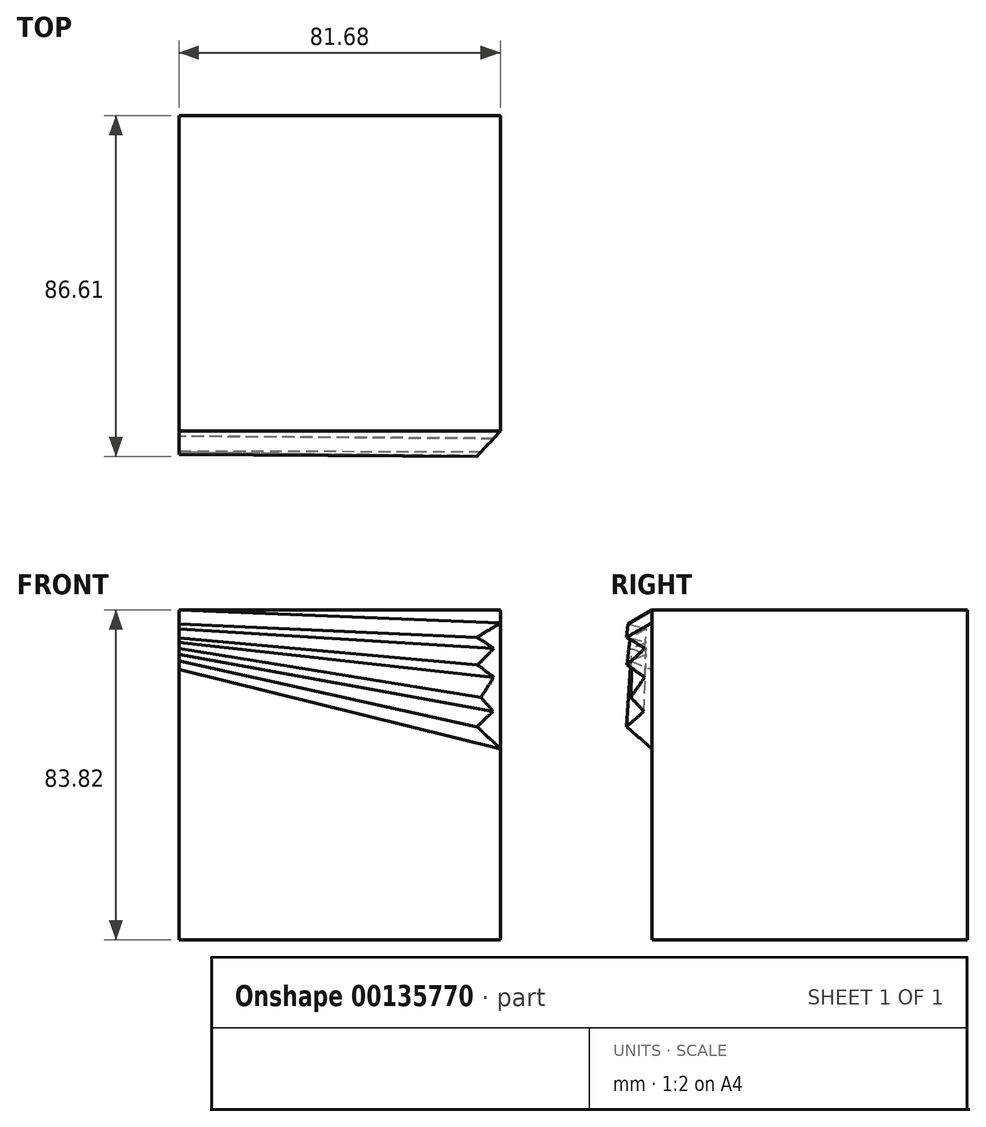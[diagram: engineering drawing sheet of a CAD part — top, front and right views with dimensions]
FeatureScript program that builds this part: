
annotation { "Feature Type Name" : "Feature", "Feature Type Description" : "" }
export const myFeature = defineFeature(function(context is Context, id is Id, definition is map)
    precondition{}
    {
        {
            var Q0;
            Q0=qCreatedBy(makeId("Top.planeOp"),FACE);
            var sketch = newSketch(context, id + "F0", { "sketchPlane" : qUnion([Q0])});
            skLineSegment(sketch, "E0.bottom", {"start": v(0, 0) * mm, "end": v(81.68, 0) * mm});
            skLineSegment(sketch, "E0.top", {"start": v(0, 80.12) * mm, "end": v(81.68, 80.12) * mm});
            skLineSegment(sketch, "E0.left", {"start": v(0, 0) * mm, "end": v(0, 80.12) * mm});
            skLineSegment(sketch, "E0.right", {"start": v(81.68, 0) * mm, "end": v(81.68, 80.12) * mm});
            skSolve(sketch);
        }
        {
            var Q0;
            Q0 = qSketchRegion(id + "F0", true);
            extrude(context, id + "F1", {"entities" : qUnion([Q0]), "depth" : 83.82 * mm});
        }
        {
            var Q0;
            Q0=makeQuery(id+"F1.opExtrude","SWEPT_FACE",FACE,{"disambiguationData":[OSD([sQuery(id+"F0.wireOp",EDGE,"E0.right")])]});
            var sketch = newSketch(context, id + "F2", { "sketchPlane" : qUnion([Q0])});
            skLineSegment(sketch, "E1", {"start": v(0, 80.54) * mm, "end": v(-6.47, 76.61) * mm});
            skLineSegment(sketch, "E2", {"start": v(-6.47, 76.61) * mm, "end": v(-1.87, 73.93) * mm});
            skLineSegment(sketch, "E3", {"start": v(-1.87, 73.93) * mm, "end": v(-6.37, 69.33) * mm});
            skLineSegment(sketch, "E4", {"start": v(-6.37, 69.33) * mm, "end": v(-1.87, 66.55) * mm});
            skLineSegment(sketch, "E5", {"start": v(-1.87, 66.55) * mm, "end": v(-5.4, 60.83) * mm});
            skLineSegment(sketch, "E6", {"start": v(-5.4, 60.83) * mm, "end": v(-2.06, 57.74) * mm});
            skLineSegment(sketch, "E7", {"start": v(-2.06, 57.74) * mm, "end": v(-6.58, 52.86) * mm});
            skLineSegment(sketch, "E8", {"start": v(-6.58, 52.86) * mm, "end": v(0, 48.55) * mm});
            skLineSegment(sketch, "E9", {"start": v(0, 48.55) * mm, "end": v(0, 80.54) * mm});
            skSolve(sketch);
        }
        {
            var Q0;
            Q0=makeQuery(id+"F1.opExtrude","SWEPT_FACE",FACE,{"disambiguationData":[OSD([sQuery(id+"F0.wireOp",EDGE,"E0.left")])]});
            var sketch = newSketch(context, id + "F3", { "sketchPlane" : qUnion([Q0])});
            skLineSegment(sketch, "E10", {"start": v(0, 83.82) * mm, "end": v(6.03, 80.24) * mm});
            skLineSegment(sketch, "E11", {"start": v(6.03, 80.24) * mm, "end": v(1.38, 79.02) * mm});
            skLineSegment(sketch, "E12", {"start": v(1.38, 79.02) * mm, "end": v(5.54, 76.72) * mm});
            skLineSegment(sketch, "E13", {"start": v(5.54, 76.72) * mm, "end": v(1.38, 75.57) * mm});
            skLineSegment(sketch, "E14", {"start": v(1.38, 75.57) * mm, "end": v(5.15, 74.03) * mm});
            skLineSegment(sketch, "E15", {"start": v(5.15, 74.03) * mm, "end": v(1.38, 72.5) * mm});
            skLineSegment(sketch, "E16", {"start": v(1.38, 72.5) * mm, "end": v(5.4, 70.84) * mm});
            skLineSegment(sketch, "E17", {"start": v(5.4, 70.84) * mm, "end": v(0, 68.66) * mm});
            skLineSegment(sketch, "E18", {"start": v(0, 68.66) * mm, "end": v(0, 83.82) * mm});
            skSolve(sketch);
        }
        {
            var Q1;
            Q1=makeQuery(id+"F2.imprint","IMPRINT",FACE,{"disambiguationData":[TD([[makeQuery(id+"F2.imprint","IMPRINT",EDGE,{"derivedFrom":sQuery(id+"F2.wireOp",EDGE,"E1")}),1.0]])]});
            var Q2;
            Q2=makeQuery(id+"F3.imprint","IMPRINT",FACE,{"disambiguationData":[TD([[makeQuery(id+"F3.imprint","IMPRINT",EDGE,{"derivedFrom":sQuery(id+"F3.wireOp",EDGE,"E10")}),-1.0]])]});
            loft(context, id + "F4", {"operationType" : NewBodyOperationType.ADD, "sheetProfilesArray" : [{ "sheetProfileEntities" : qUnion([Q1]) }, { "sheetProfileEntities" : qUnion([Q2]) }]});
        }
        {
            var Q0;
            Q0=makeQuery(id+"F1.opExtrude","CAP_FACE",FACE,{"disambiguationData":[OSD([sQuery(id+"F0.wireOp",EDGE,"E0.bottom"),sQuery(id+"F0.wireOp",EDGE,"E0.top"),sQuery(id+"F0.wireOp",EDGE,"E0.left"),sQuery(id+"F0.wireOp",EDGE,"E0.right")])],"isStart":false});
            var sketch = newSketch(context, id + "F5", { "sketchPlane" : qUnion([Q0])});
            skLineSegment(sketch, "E19", {"start": v(81.68, 0) * mm, "end": v(73.98, -8.36) * mm});
            skLineSegment(sketch, "E20", {"start": v(73.98, -8.36) * mm, "end": v(83.87, -8.36) * mm});
            skLineSegment(sketch, "E21", {"start": v(83.87, -8.36) * mm, "end": v(81.68, 0) * mm});
            skSolve(sketch);
        }
        {
            var Q0;
            Q0=makeQuery(id+"F5.imprint","IMPRINT",FACE,{"disambiguationData":[TD([[makeQuery(id+"F5.imprint","IMPRINT",EDGE,{"derivedFrom":sQuery(id+"F5.wireOp",EDGE,"E19")}),1.0]])]});
            extrude(context, id + "F6", {"entities" : qUnion([Q0]), "operationType" : NewBodyOperationType.REMOVE, "endBound" : BoundingType.THROUGH_ALL, "oppositeDirection" : true, "depth" : 25.4 * mm});
        }
    });
